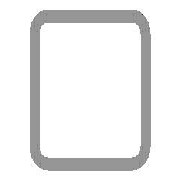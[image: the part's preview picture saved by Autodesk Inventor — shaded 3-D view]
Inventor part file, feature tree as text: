
AUTODESK INVENTOR PART (.ipt)
format: ipt  version: 2018 (Build 220112000, 112)  size: 144,384 bytes
history: native  units: mm (DEFAULTED — no unit token found)
features: other x4, sketch x4, extrude x2, plane x1
ambient origin geometry x8: Origin, YZ Plane, XZ Plane, XY Plane, X Axis, Y Axis, Z Axis, Center Point
bodies: Solid1 (feature_tree)
feature tree (11):
  other  "Tubolare verticale 45 - Taglio"
  other  "Driven Length"
  other  "Piano iniziale"
  other  "Piano finale"
  extrude  "Corpo"  TaperAngle=0.0deg  [1 undecoded]
  extrude  "Estrusione2"  Depth=40.0mm
  sketch  "Schizzo"
  sketch  "Sketch3"  dims[d3=900.0mm d4=0.0mm]
  plane  "Work Plane3"
  sketch  "Sketch4"  dims[d7=4.0mm d9=40.0mm d11=40.0mm d12=2.0mm d13=-0.0mm d14=900.0mm d15=20.0mm d16=20.0mm d17=90.0deg d18=900.0mm d19=45.0deg d20=10.0mm d21=0.0mm]
  sketch  "Schizzo5"
note: 1 required parameter value undecoded (feature->parameter linkage not recoverable at this tier; creation-order binding heuristic only, values carry confidence <= 0.55)
